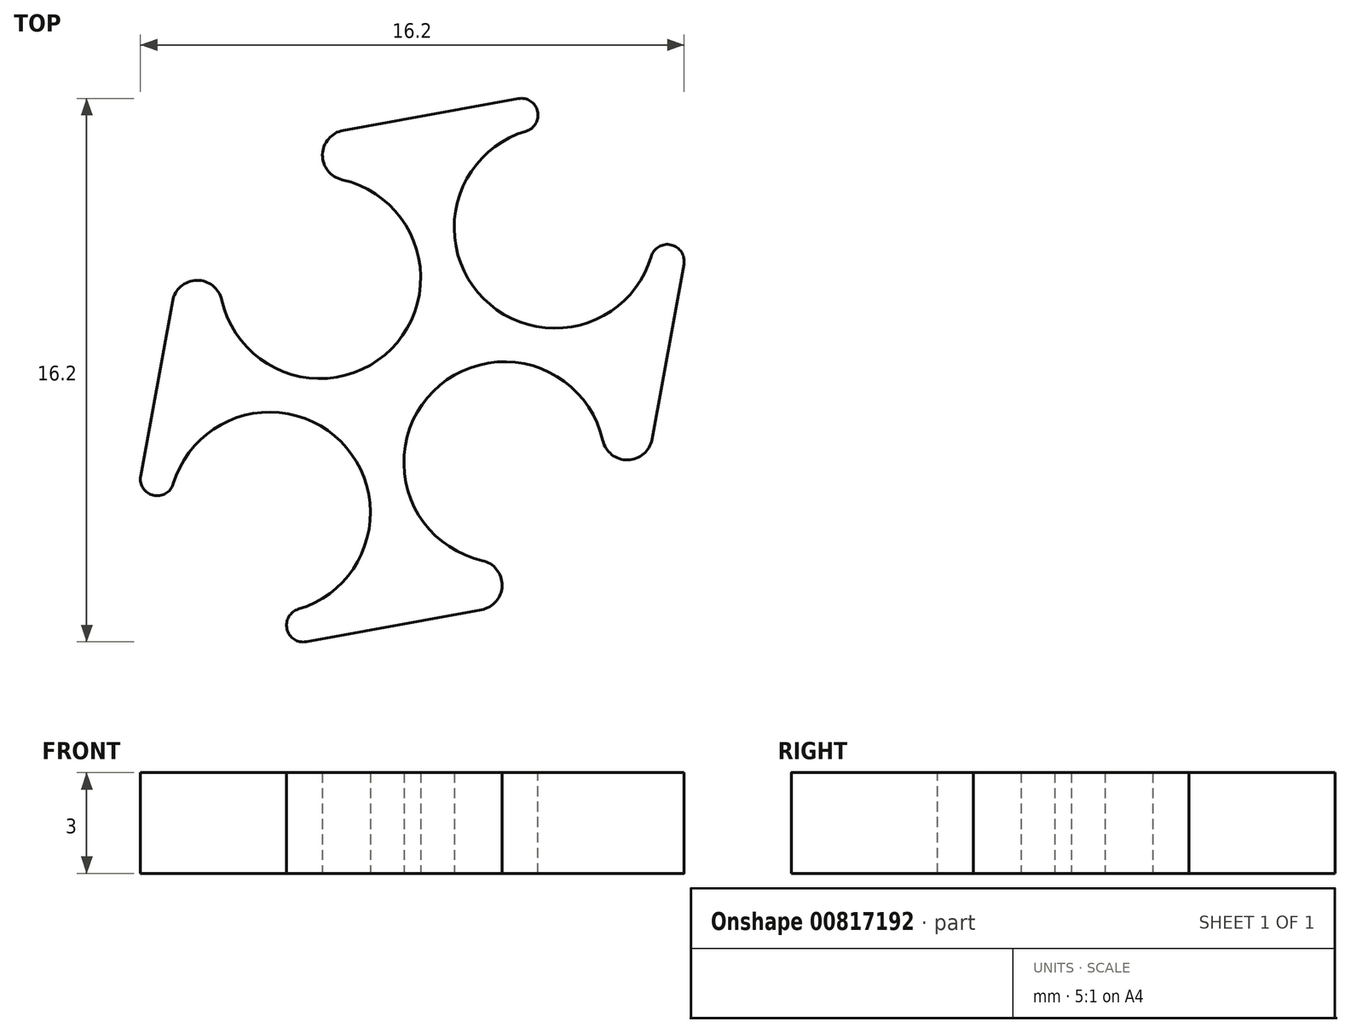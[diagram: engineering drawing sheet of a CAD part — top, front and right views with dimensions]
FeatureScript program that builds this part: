
annotation { "Feature Type Name" : "Feature", "Feature Type Description" : "" }
export const myFeature = defineFeature(function(context is Context, id is Id, definition is map)
    precondition{}
    {
        {
            var Q0;
            Q0=qCreatedBy(makeId("Top.planeOp"),FACE);
            var sketch = newSketch(context, id + "F0", { "sketchPlane" : qUnion([Q0])});
            skCircle(sketch, "E0", {"center": v(4.25, 4.25) * mm, "radius": 3 * mm});
            skCircle(sketch, "E1.1.0", {"center": v(-4.25, -4.25) * mm, "radius": 3 * mm});
            skPoint(sketch, "E1.center", {"position": v(0, 0) * mm});
            skCircle(sketch, "E2", {"center": v(-2.75, 2.75) * mm, "radius": 3 * mm});
            skCircle(sketch, "E3.1.0", {"center": v(2.75, -2.75) * mm, "radius": 3 * mm});
            skLineSegment(sketch, "E4", {"start": v(-6.36, 6.36) * mm, "end": v(6.36, -6.36) * mm, "construction": true});
            skLineSegment(sketch, "E5", {"start": v(-9.2, -9.2) * mm, "end": v(9.2, 9.2) * mm, "construction": true});
            skLineSegment(sketch, "E6", {"start": v(-6.36, 6.36) * mm, "end": v(9.2, 9.2) * mm});
            skLineSegment(sketch, "E7", {"start": v(6.36, -6.36) * mm, "end": v(-9.2, -9.2) * mm});
            skLineSegment(sketch, "E8", {"start": v(-6.36, 6.36) * mm, "end": v(-9.2, -9.2) * mm});
            skLineSegment(sketch, "E9", {"start": v(9.2, 9.2) * mm, "end": v(6.36, -6.36) * mm});
            skLineSegment(sketch, "E10", {"start": v(-4.25, -4.25) * mm, "end": v(-8.58, -5.83) * mm});
            skLineSegment(sketch, "E11", {"start": v(-2.75, 2.75) * mm, "end": v(-4.2, 6.76) * mm});
            skLineSegment(sketch, "E12.MirrorCS", {"start": v(-2.75, 2.75) * mm, "end": v(-6.76, 4.2) * mm});
            skLineSegment(sketch, "E13.MirrorCS", {"start": v(-4.25, -4.25) * mm, "end": v(-5.83, -8.58) * mm});
            skLineSegment(sketch, "E14.MirrorCS", {"start": v(4.25, 4.25) * mm, "end": v(5.83, 8.58) * mm});
            skLineSegment(sketch, "E15.MirrorCS", {"start": v(4.25, 4.25) * mm, "end": v(8.58, 5.83) * mm});
            skLineSegment(sketch, "E16.MirrorCS", {"start": v(2.75, -2.75) * mm, "end": v(6.76, -4.2) * mm});
            skLineSegment(sketch, "E17.MirrorCS", {"start": v(2.75, -2.75) * mm, "end": v(4.2, -6.76) * mm});
            skSolve(sketch);
        }
        {
            var Q0;
            {var subQ10=sQuery(id+"F0.wireOp",EDGE,"E14.MirrorCS");var subQ21=sQuery(id+"F0.wireOp",EDGE,"E0");var subQ22=makeQuery(id+"F0.imprint","INTERSECT",VERTEX,{"derivedFrom":[subQ21,subQ10]});Q0=makeQuery(id+"F0.imprint","IMPRINT",FACE,{"disambiguationData":[TD([[makeQuery(id+"F0.imprint","IMPRINT",EDGE,{"disambiguationData":[TD([[subQ22,-1.0]])],"derivedFrom":subQ21}),-1.0]])]});}
            extrude(context, id + "F1", {"entities" : qUnion([Q0]), "depth" : 3 * mm, "offsetDistance" : 25 * mm});
        }
        {
            var Q0;
            Q0=makeQuery(id+"F1.opExtrude","SWEPT_EDGE",EDGE,{"disambiguationData":[OSD([sQuery(id+"F0.wireOp",EDGE,"E9"),sQuery(id+"F0.wireOp",EDGE,"E16.MirrorCS")])]});
            var Q1;
            Q1=makeQuery(id+"F1.opExtrude","SWEPT_EDGE",EDGE,{"disambiguationData":[OSD([sQuery(id+"F0.wireOp",EDGE,"E7"),sQuery(id+"F0.wireOp",EDGE,"E17.MirrorCS")])]});
            var Q2;
            Q2=makeQuery(id+"F1.opExtrude","SWEPT_EDGE",EDGE,{"disambiguationData":[OSD([sQuery(id+"F0.wireOp",EDGE,"E9"),sQuery(id+"F0.wireOp",EDGE,"E15.MirrorCS")])]});
            var Q3;
            Q3=makeQuery(id+"F1.opExtrude","SWEPT_EDGE",EDGE,{"disambiguationData":[OSD([sQuery(id+"F0.wireOp",EDGE,"E6"),sQuery(id+"F0.wireOp",EDGE,"E14.MirrorCS")])]});
            var Q4;
            Q4=makeQuery(id+"F1.opExtrude","SWEPT_EDGE",EDGE,{"disambiguationData":[OSD([sQuery(id+"F0.wireOp",EDGE,"E6"),sQuery(id+"F0.wireOp",EDGE,"E11")])]});
            var Q5;
            Q5=makeQuery(id+"F1.opExtrude","SWEPT_EDGE",EDGE,{"disambiguationData":[OSD([sQuery(id+"F0.wireOp",EDGE,"E8"),sQuery(id+"F0.wireOp",EDGE,"E12.MirrorCS")])]});
            var Q6;
            Q6=makeQuery(id+"F1.opExtrude","SWEPT_EDGE",EDGE,{"disambiguationData":[OSD([sQuery(id+"F0.wireOp",EDGE,"E8"),sQuery(id+"F0.wireOp",EDGE,"E10")])]});
            var Q7;
            Q7=makeQuery(id+"F1.opExtrude","SWEPT_EDGE",EDGE,{"disambiguationData":[OSD([sQuery(id+"F0.wireOp",EDGE,"E7"),sQuery(id+"F0.wireOp",EDGE,"E13.MirrorCS")])]});
            fillet(context, id + "F2", {"entities" : qUnion([Q0, Q1, Q2, Q3, Q4, Q5, Q6, Q7]), "radius" : 2 * mm, "tangentPropagation" : true, "allowEdgeOverflow" : false});
        }
        {
            var Q0;
            Q0=makeQuery(id+"F2.opFillet","BLEND_EDGE",EDGE,{"blendedFrom":[makeQuery(id+"F1.opExtrude","SWEPT_EDGE",EDGE,{"disambiguationData":[OSD([sQuery(id+"F0.wireOp",EDGE,"E7"),sQuery(id+"F0.wireOp",EDGE,"E13.MirrorCS")])]}),makeQuery(id+"F1.opExtrude","SWEPT_FACE",FACE,{"disambiguationData":[OSD([sQuery(id+"F0.wireOp",EDGE,"E1.1.0")])]})],"blendedInto":[makeQuery(id+"F1.opExtrude","SWEPT_FACE",FACE,{"disambiguationData":[OSD([sQuery(id+"F0.wireOp",EDGE,"E1.1.0")])]})]});
            var Q1;
            Q1=makeQuery(id+"F2.opFillet","BLEND_EDGE",EDGE,{"blendedFrom":[makeQuery(id+"F1.opExtrude","SWEPT_EDGE",EDGE,{"disambiguationData":[OSD([sQuery(id+"F0.wireOp",EDGE,"E8"),sQuery(id+"F0.wireOp",EDGE,"E10")])]}),makeQuery(id+"F1.opExtrude","SWEPT_FACE",FACE,{"disambiguationData":[OSD([sQuery(id+"F0.wireOp",EDGE,"E1.1.0")])]})],"blendedInto":[makeQuery(id+"F1.opExtrude","SWEPT_FACE",FACE,{"disambiguationData":[OSD([sQuery(id+"F0.wireOp",EDGE,"E1.1.0")])]})]});
            var Q2;
            Q2=makeQuery(id+"F2.opFillet","BLEND_EDGE",EDGE,{"blendedFrom":[makeQuery(id+"F1.opExtrude","SWEPT_EDGE",EDGE,{"disambiguationData":[OSD([sQuery(id+"F0.wireOp",EDGE,"E6"),sQuery(id+"F0.wireOp",EDGE,"E14.MirrorCS")])]}),makeQuery(id+"F1.opExtrude","SWEPT_FACE",FACE,{"disambiguationData":[OSD([sQuery(id+"F0.wireOp",EDGE,"E0")])]})],"blendedInto":[makeQuery(id+"F1.opExtrude","SWEPT_FACE",FACE,{"disambiguationData":[OSD([sQuery(id+"F0.wireOp",EDGE,"E0")])]})]});
            var Q3;
            Q3=makeQuery(id+"F2.opFillet","BLEND_EDGE",EDGE,{"blendedFrom":[makeQuery(id+"F1.opExtrude","SWEPT_EDGE",EDGE,{"disambiguationData":[OSD([sQuery(id+"F0.wireOp",EDGE,"E9"),sQuery(id+"F0.wireOp",EDGE,"E15.MirrorCS")])]}),makeQuery(id+"F1.opExtrude","SWEPT_FACE",FACE,{"disambiguationData":[OSD([sQuery(id+"F0.wireOp",EDGE,"E0")])]})],"blendedInto":[makeQuery(id+"F1.opExtrude","SWEPT_FACE",FACE,{"disambiguationData":[OSD([sQuery(id+"F0.wireOp",EDGE,"E0")])]})]});
            fillet(context, id + "F3", {"entities" : qUnion([Q0, Q1, Q2, Q3]), "radius" : 0.5 * mm, "tangentPropagation" : true, "allowEdgeOverflow" : false});
        }
        {
            var Q0;
            Q0=makeQuery(id+"F2.opFillet","BLEND_EDGE",EDGE,{"blendedFrom":[makeQuery(id+"F1.opExtrude","SWEPT_EDGE",EDGE,{"disambiguationData":[OSD([sQuery(id+"F0.wireOp",EDGE,"E8"),sQuery(id+"F0.wireOp",EDGE,"E12.MirrorCS")])]}),makeQuery(id+"F1.opExtrude","SWEPT_FACE",FACE,{"disambiguationData":[OSD([sQuery(id+"F0.wireOp",EDGE,"E2")])]})],"blendedInto":[makeQuery(id+"F1.opExtrude","SWEPT_FACE",FACE,{"disambiguationData":[OSD([sQuery(id+"F0.wireOp",EDGE,"E2")])]})]});
            var Q1;
            Q1=makeQuery(id+"F2.opFillet","BLEND_EDGE",EDGE,{"blendedFrom":[makeQuery(id+"F1.opExtrude","SWEPT_EDGE",EDGE,{"disambiguationData":[OSD([sQuery(id+"F0.wireOp",EDGE,"E6"),sQuery(id+"F0.wireOp",EDGE,"E11")])]}),makeQuery(id+"F1.opExtrude","SWEPT_FACE",FACE,{"disambiguationData":[OSD([sQuery(id+"F0.wireOp",EDGE,"E2")])]})],"blendedInto":[makeQuery(id+"F1.opExtrude","SWEPT_FACE",FACE,{"disambiguationData":[OSD([sQuery(id+"F0.wireOp",EDGE,"E2")])]})]});
            var Q2;
            Q2=makeQuery(id+"F2.opFillet","BLEND_EDGE",EDGE,{"blendedFrom":[makeQuery(id+"F1.opExtrude","SWEPT_EDGE",EDGE,{"disambiguationData":[OSD([sQuery(id+"F0.wireOp",EDGE,"E7"),sQuery(id+"F0.wireOp",EDGE,"E17.MirrorCS")])]}),makeQuery(id+"F1.opExtrude","SWEPT_FACE",FACE,{"disambiguationData":[OSD([sQuery(id+"F0.wireOp",EDGE,"E3.1.0")])]})],"blendedInto":[makeQuery(id+"F1.opExtrude","SWEPT_FACE",FACE,{"disambiguationData":[OSD([sQuery(id+"F0.wireOp",EDGE,"E3.1.0")])]})]});
            var Q3;
            Q3=makeQuery(id+"F2.opFillet","BLEND_EDGE",EDGE,{"blendedFrom":[makeQuery(id+"F1.opExtrude","SWEPT_EDGE",EDGE,{"disambiguationData":[OSD([sQuery(id+"F0.wireOp",EDGE,"E9"),sQuery(id+"F0.wireOp",EDGE,"E16.MirrorCS")])]}),makeQuery(id+"F1.opExtrude","SWEPT_FACE",FACE,{"disambiguationData":[OSD([sQuery(id+"F0.wireOp",EDGE,"E3.1.0")])]})],"blendedInto":[makeQuery(id+"F1.opExtrude","SWEPT_FACE",FACE,{"disambiguationData":[OSD([sQuery(id+"F0.wireOp",EDGE,"E3.1.0")])]})]});
            fillet(context, id + "F4", {"entities" : qUnion([Q0, Q1, Q2, Q3]), "radius" : 0.75 * mm, "tangentPropagation" : true, "allowEdgeOverflow" : false});
        }
    });
